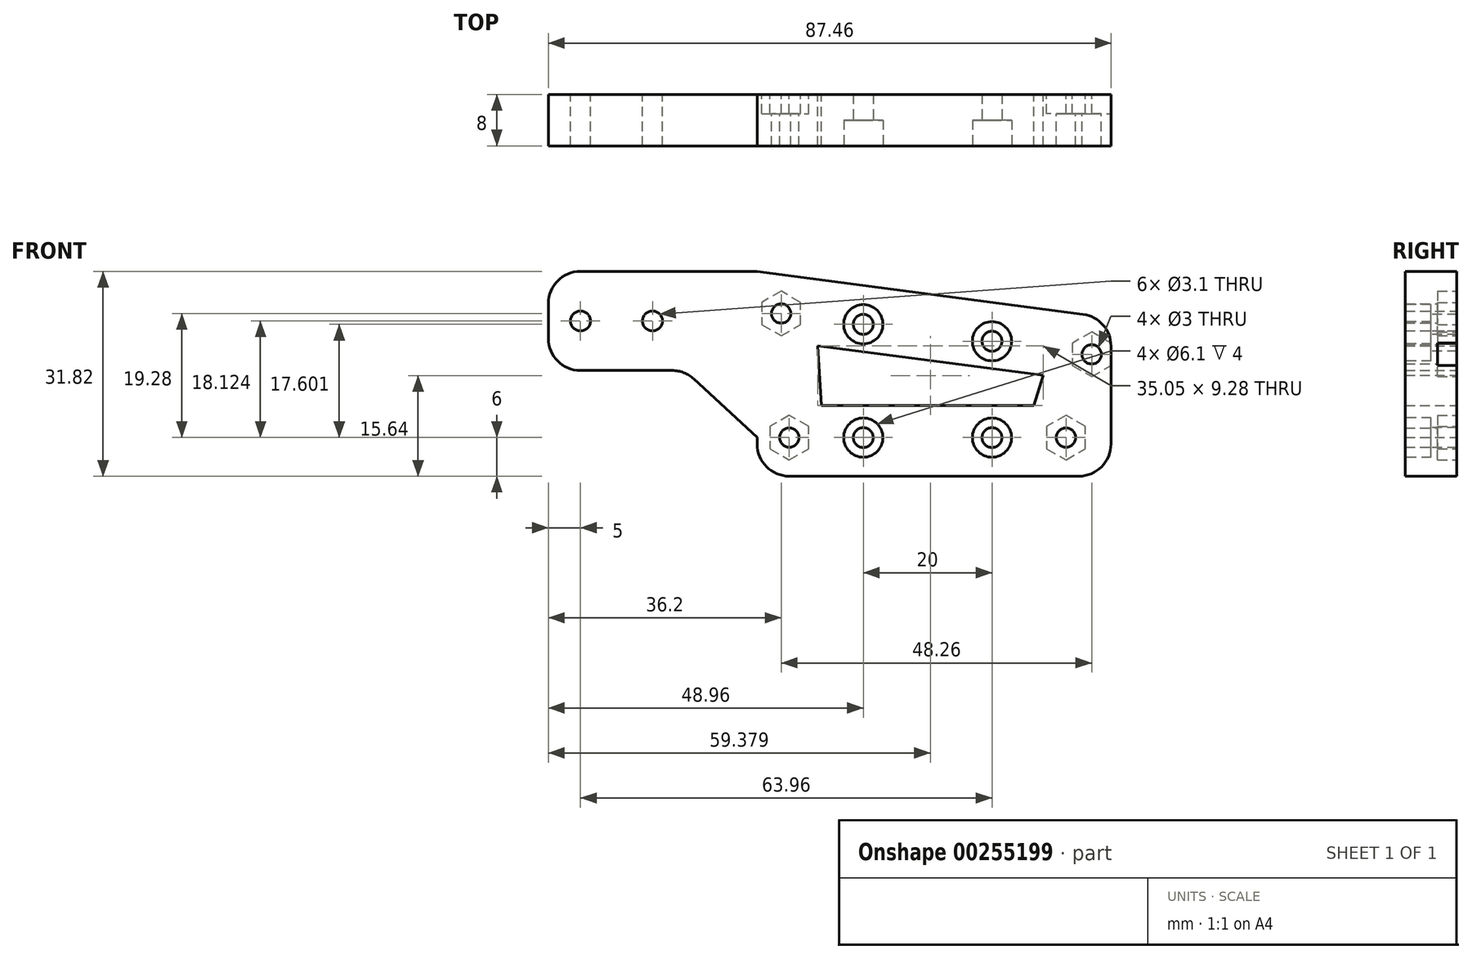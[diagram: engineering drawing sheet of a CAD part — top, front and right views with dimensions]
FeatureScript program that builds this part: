
annotation { "Feature Type Name" : "Feature", "Feature Type Description" : "" }
export const myFeature = defineFeature(function(context is Context, id is Id, definition is map)
    precondition{}
    {
        {
            var Q0;
            Q0=qCreatedBy(makeId("Front.planeOp"),FACE);
            var sketch = newSketch(context, id + "F0", { "sketchPlane" : qUnion([Q0])});
            skCircle(sketch, "E0", {"center": v(5, 0) * mm, "radius": 1.5 * mm});
            skCircle(sketch, "E1", {"center": v(3.74, 19.28) * mm, "radius": 1.5 * mm});
            skCircle(sketch, "E2", {"center": v(48, 0) * mm, "radius": 1.5 * mm});
            skCircle(sketch, "E3", {"center": v(52, 12.93) * mm, "radius": 1.5 * mm});
            skLineSegment(sketch, "E4", {"start": v(0, -6) * mm, "end": v(0, 0) * mm, "construction": true});
            skLineSegment(sketch, "E5", {"start": v(55, 18.59) * mm, "end": v(55, -6) * mm, "construction": true});
            skLineSegment(sketch, "E6", {"start": v(3.74, 25.33) * mm, "end": v(3.74, 19.28) * mm, "construction": true});
            skLineSegment(sketch, "E7", {"start": v(52, 18.98) * mm, "end": v(52, 12.93) * mm, "construction": true});
            skLineSegment(sketch, "E8", {"start": v(0, 10.42) * mm, "end": v(0, 9.91) * mm, "construction": true});
            skLineSegment(sketch, "E9", {"start": v(55, 18.59) * mm, "end": v(55, -6) * mm});
            skLineSegment(sketch, "E10.bottom", {"start": v(0, -6) * mm, "end": v(55, -6) * mm});
            skLineSegment(sketch, "E11", {"start": v(3.74, 19.28) * mm, "end": v(52, 12.93) * mm, "construction": true});
            skLineSegment(sketch, "E12", {"start": v(5, 0) * mm, "end": v(48, 0) * mm, "construction": true});
            skLineSegment(sketch, "E13", {"start": v(55, 18.59) * mm, "end": v(0, 25.82) * mm});
            skLineSegment(sketch, "E14", {"start": v(3.74, 19.28) * mm, "end": v(5, 0) * mm, "construction": true});
            skLineSegment(sketch, "E15", {"start": v(52, 12.93) * mm, "end": v(48, 0) * mm, "construction": true});
            skLineSegment(sketch, "E16", {"start": v(9.4, 14.28) * mm, "end": v(44.44, 9.67) * mm});
            skLineSegment(sketch, "E17", {"start": v(44.44, 9.67) * mm, "end": v(43, 5) * mm});
            skLineSegment(sketch, "E18", {"start": v(43, 5) * mm, "end": v(10, 5) * mm});
            skLineSegment(sketch, "E19", {"start": v(10, 5) * mm, "end": v(9.4, 14.28) * mm});
            skPoint(sketch, "E20.orphan", {"position": v(0, -10.57) * mm});
            skPoint(sketch, "E21.orphan", {"position": v(55, -10.57) * mm});
            skPoint(sketch, "E22.orphan", {"position": v(55, 37.93) * mm});
            skPoint(sketch, "E23.orphan", {"position": v(52, 32.93) * mm});
            skPoint(sketch, "E24.orphan", {"position": v(55, 31.16) * mm});
            skPoint(sketch, "E25.orphan", {"position": v(3.74, 39.28) * mm});
            skPoint(sketch, "E26.orphan", {"position": v(0, 44.28) * mm});
            skPoint(sketch, "E27.orphan", {"position": v(0, 31.16) * mm});
            skLineSegment(sketch, "E28", {"start": v(3.74, 18.12) * mm, "end": v(-11.26, 18.12) * mm, "construction": true});
            skLineSegment(sketch, "E29", {"start": v(-11.26, 18.12) * mm, "end": v(-32.46, 18.12) * mm, "construction": true});
            skLineSegment(sketch, "E30", {"start": v(0, 25.82) * mm, "end": v(-32.46, 25.82) * mm});
            skLineSegment(sketch, "E31", {"start": v(-32.46, 25.82) * mm, "end": v(-32.46, 18.12) * mm});
            skCircle(sketch, "E32", {"center": v(-27.46, 18.12) * mm, "radius": 1.55 * mm});
            skLineSegment(sketch, "E33", {"start": v(-21.86, 18.12) * mm, "end": v(-21.86, 25.82) * mm, "construction": true});
            skCircle(sketch, "E34.MirrorC", {"center": v(-16.26, 18.12) * mm, "radius": 1.55 * mm});
            skLineSegment(sketch, "E35", {"start": v(-32.46, 18.12) * mm, "end": v(-32.46, 10.42) * mm});
            skPoint(sketch, "E36.endSnap0", {"position": v(0, 9.91) * mm});
            skLineSegment(sketch, "E37", {"start": v(-32.46, 10.42) * mm, "end": v(-11.26, 10.42) * mm});
            skLineSegment(sketch, "E38", {"start": v(-11.26, 10.42) * mm, "end": v(0, 0) * mm});
            skLineSegment(sketch, "E39.trimOffspring", {"start": v(0, 0) * mm, "end": v(0, -6) * mm});
            skSolve(sketch);
        }
        {
            var Q0;
            Q0 = qSketchRegion(id + "F0", true);
            extrude(context, id + "F1", {"entities" : qUnion([Q0]), "depth" : 8 * mm});
        }
        {
            var Q0;
            Q0=makeQuery(id+"F1.opExtrude","CAP_FACE",FACE,{"disambiguationData":[OSD([sQuery(id+"F0.wireOp",EDGE,"E0"),sQuery(id+"F0.wireOp",EDGE,"E1"),sQuery(id+"F0.wireOp",EDGE,"E2"),sQuery(id+"F0.wireOp",EDGE,"E3"),sQuery(id+"F0.wireOp",EDGE,"E8"),sQuery(id+"F0.wireOp",EDGE,"E9"),sQuery(id+"F0.wireOp",EDGE,"E10.bottom"),sQuery(id+"F0.wireOp",EDGE,"E13"),sQuery(id+"F0.wireOp",EDGE,"E16"),sQuery(id+"F0.wireOp",EDGE,"E17"),sQuery(id+"F0.wireOp",EDGE,"E18"),sQuery(id+"F0.wireOp",EDGE,"E19")])],"isStart":true});
            var sketch = newSketch(context, id + "F2", { "sketchPlane" : qUnion([Q0])});
            skCircle(sketch, "E40.cCircle", {"center": v(-52, 12.93) * mm, "radius": 3 * mm, "construction": true});
            skLineSegment(sketch, "E40.0", {"start": v(-49, 14.66) * mm, "end": v(-49, 11.2) * mm});
            skLineSegment(sketch, "E40.1", {"start": v(-49, 11.2) * mm, "end": v(-52, 9.47) * mm});
            skLineSegment(sketch, "E40.2", {"start": v(-52, 9.47) * mm, "end": v(-55, 11.2) * mm});
            skLineSegment(sketch, "E40.3", {"start": v(-55, 11.2) * mm, "end": v(-55, 14.66) * mm});
            skLineSegment(sketch, "E40.4", {"start": v(-55, 14.66) * mm, "end": v(-52, 16.4) * mm});
            skLineSegment(sketch, "E40.5", {"start": v(-52, 16.4) * mm, "end": v(-49, 14.66) * mm});
            skPoint(sketch, "E40.0.midPoint", {"position": v(-49, 12.93) * mm});
            skCircle(sketch, "E41.cCircle", {"center": v(-48, 0) * mm, "radius": 3 * mm, "construction": true});
            skLineSegment(sketch, "E41.0", {"start": v(-45, 1.73) * mm, "end": v(-45, -1.73) * mm});
            skLineSegment(sketch, "E41.1", {"start": v(-45, -1.73) * mm, "end": v(-48, -3.46) * mm});
            skLineSegment(sketch, "E41.2", {"start": v(-48, -3.46) * mm, "end": v(-51, -1.73) * mm});
            skLineSegment(sketch, "E41.3", {"start": v(-51, -1.73) * mm, "end": v(-51, 1.73) * mm});
            skLineSegment(sketch, "E41.4", {"start": v(-51, 1.73) * mm, "end": v(-48, 3.46) * mm});
            skLineSegment(sketch, "E41.5", {"start": v(-48, 3.46) * mm, "end": v(-45, 1.73) * mm});
            skPoint(sketch, "E41.0.midPoint", {"position": v(-45, 0) * mm});
            skCircle(sketch, "E42.cCircle", {"center": v(-5, 0) * mm, "radius": 3 * mm, "construction": true});
            skLineSegment(sketch, "E42.0", {"start": v(-8, -1.73) * mm, "end": v(-8, 1.73) * mm});
            skLineSegment(sketch, "E42.1", {"start": v(-8, 1.73) * mm, "end": v(-5, 3.46) * mm});
            skLineSegment(sketch, "E42.2", {"start": v(-5, 3.46) * mm, "end": v(-2, 1.73) * mm});
            skLineSegment(sketch, "E42.3", {"start": v(-2, 1.73) * mm, "end": v(-2, -1.73) * mm});
            skLineSegment(sketch, "E42.4", {"start": v(-2, -1.73) * mm, "end": v(-5, -3.46) * mm});
            skLineSegment(sketch, "E42.5", {"start": v(-5, -3.46) * mm, "end": v(-8, -1.73) * mm});
            skPoint(sketch, "E42.0.midPoint", {"position": v(-8, 0) * mm});
            skCircle(sketch, "E43.cCircle", {"center": v(-3.74, 19.28) * mm, "radius": 3 * mm, "construction": true});
            skLineSegment(sketch, "E43.0", {"start": v(-6.74, 17.55) * mm, "end": v(-6.74, 21.01) * mm});
            skLineSegment(sketch, "E43.1", {"start": v(-6.74, 21.01) * mm, "end": v(-3.74, 22.74) * mm});
            skLineSegment(sketch, "E43.2", {"start": v(-3.74, 22.74) * mm, "end": v(-0.74, 21.01) * mm});
            skLineSegment(sketch, "E43.3", {"start": v(-0.74, 21.01) * mm, "end": v(-0.74, 17.55) * mm});
            skLineSegment(sketch, "E43.4", {"start": v(-0.74, 17.55) * mm, "end": v(-3.74, 15.82) * mm});
            skLineSegment(sketch, "E43.5", {"start": v(-3.74, 15.82) * mm, "end": v(-6.74, 17.55) * mm});
            skPoint(sketch, "E43.0.midPoint", {"position": v(-6.74, 19.28) * mm});
            skSolve(sketch);
        }
        {
            var Q0;
            Q0 = qSketchRegion(id + "F2", true);
            extrude(context, id + "F3", {"entities" : qUnion([Q0]), "operationType" : NewBodyOperationType.REMOVE, "oppositeDirection" : true, "depth" : 3 * mm});
        }
        {
            var Q0;
            Q0=makeQuery(id+"F1.opExtrude","CAP_FACE",FACE,{"disambiguationData":[OSD([sQuery(id+"F0.wireOp",EDGE,"E0"),sQuery(id+"F0.wireOp",EDGE,"E1"),sQuery(id+"F0.wireOp",EDGE,"E2"),sQuery(id+"F0.wireOp",EDGE,"E3"),sQuery(id+"F0.wireOp",EDGE,"E8"),sQuery(id+"F0.wireOp",EDGE,"E9"),sQuery(id+"F0.wireOp",EDGE,"E10.bottom"),sQuery(id+"F0.wireOp",EDGE,"E13"),sQuery(id+"F0.wireOp",EDGE,"E16"),sQuery(id+"F0.wireOp",EDGE,"E17"),sQuery(id+"F0.wireOp",EDGE,"E18"),sQuery(id+"F0.wireOp",EDGE,"E19")])],"isStart":false});
            var sketch = newSketch(context, id + "F4", { "sketchPlane" : qUnion([Q0])});
            skLineSegment(sketch, "E44", {"start": v(5, 0) * mm, "end": v(48, 0) * mm, "construction": true});
            skLineSegment(sketch, "E45", {"start": v(3.74, 19.28) * mm, "end": v(52, 12.93) * mm, "construction": true});
            skCircle(sketch, "E46", {"center": v(16.5, 0) * mm, "radius": 1.55 * mm});
            skCircle(sketch, "E47", {"center": v(36.5, 0) * mm, "radius": 1.55 * mm});
            skLineSegment(sketch, "E48", {"start": v(16.5, 0) * mm, "end": v(16.5, 17.6) * mm, "construction": true});
            skLineSegment(sketch, "E49", {"start": v(36.5, 0) * mm, "end": v(36.5, 14.97) * mm, "construction": true});
            skCircle(sketch, "E50", {"center": v(16.5, 17.6) * mm, "radius": 1.55 * mm});
            skCircle(sketch, "E51", {"center": v(36.5, 14.97) * mm, "radius": 1.55 * mm});
            skSolve(sketch);
        }
        {
            var Q0;
            Q0 = qSketchRegion(id + "F4", true);
            extrude(context, id + "F5", {"entities" : qUnion([Q0]), "operationType" : NewBodyOperationType.REMOVE, "endBound" : BoundingType.THROUGH_ALL, "oppositeDirection" : true, "depth" : 4.2 * mm});
        }
        {
            var Q0;
            Q0=makeQuery(id+"F1.opExtrude","CAP_FACE",FACE,{"disambiguationData":[OSD([sQuery(id+"F0.wireOp",EDGE,"E0"),sQuery(id+"F0.wireOp",EDGE,"E1"),sQuery(id+"F0.wireOp",EDGE,"E2"),sQuery(id+"F0.wireOp",EDGE,"E3"),sQuery(id+"F0.wireOp",EDGE,"E8"),sQuery(id+"F0.wireOp",EDGE,"E9"),sQuery(id+"F0.wireOp",EDGE,"E10.bottom"),sQuery(id+"F0.wireOp",EDGE,"E13"),sQuery(id+"F0.wireOp",EDGE,"E16"),sQuery(id+"F0.wireOp",EDGE,"E17"),sQuery(id+"F0.wireOp",EDGE,"E18"),sQuery(id+"F0.wireOp",EDGE,"E19")])],"isStart":false});
            var sketch = newSketch(context, id + "F6", { "sketchPlane" : qUnion([Q0])});
            skCircle(sketch, "E52", {"center": v(16.5, 0) * mm, "radius": 3.05 * mm});
            skCircle(sketch, "E53", {"center": v(36.5, 0) * mm, "radius": 3.05 * mm});
            skCircle(sketch, "E54", {"center": v(16.5, 17.6) * mm, "radius": 3.05 * mm});
            skCircle(sketch, "E55", {"center": v(36.5, 14.97) * mm, "radius": 3.05 * mm});
            skSolve(sketch);
        }
        {
            var Q0;
            Q0 = qSketchRegion(id + "F6", true);
            extrude(context, id + "F7", {"entities" : qUnion([Q0]), "operationType" : NewBodyOperationType.REMOVE, "oppositeDirection" : true, "depth" : 4 * mm});
        }
        {
            var Q0;
            Q0=makeQuery(id+"F1.opExtrude","SWEPT_EDGE",EDGE,{"disambiguationData":[OSD([sQuery(id+"F0.wireOp",EDGE,"E30"),sQuery(id+"F0.wireOp",EDGE,"E31")])]});
            var Q1;
            Q1=makeQuery(id+"F1.opExtrude","SWEPT_EDGE",EDGE,{"disambiguationData":[OSD([sQuery(id+"F0.wireOp",EDGE,"E35"),sQuery(id+"F0.wireOp",EDGE,"E37")])]});
            var Q2;
            Q2=makeQuery(id+"F1.opExtrude","SWEPT_EDGE",EDGE,{"disambiguationData":[OSD([sQuery(id+"F0.wireOp",EDGE,"E37"),sQuery(id+"F0.wireOp",EDGE,"E38")])]});
            var Q3;
            Q3=makeQuery(id+"F1.opExtrude","SWEPT_EDGE",EDGE,{"disambiguationData":[OSD([sQuery(id+"F0.wireOp",EDGE,"E10.bottom"),sQuery(id+"F0.wireOp",EDGE,"E39.trimOffspring")])]});
            var Q4;
            Q4=makeQuery(id+"F1.opExtrude","SWEPT_EDGE",EDGE,{"disambiguationData":[OSD([sQuery(id+"F0.wireOp",EDGE,"E9"),sQuery(id+"F0.wireOp",EDGE,"E10.bottom")])]});
            var Q5;
            Q5=makeQuery(id+"F1.opExtrude","SWEPT_EDGE",EDGE,{"disambiguationData":[OSD([sQuery(id+"F0.wireOp",EDGE,"E9"),sQuery(id+"F0.wireOp",EDGE,"E13")])]});
            fillet(context, id + "F8", {"entities" : qUnion([Q0, Q1, Q2, Q3, Q4, Q5]), "radius" : 5 * mm, "tangentPropagation" : true, "allowEdgeOverflow" : false});
        }
    });
